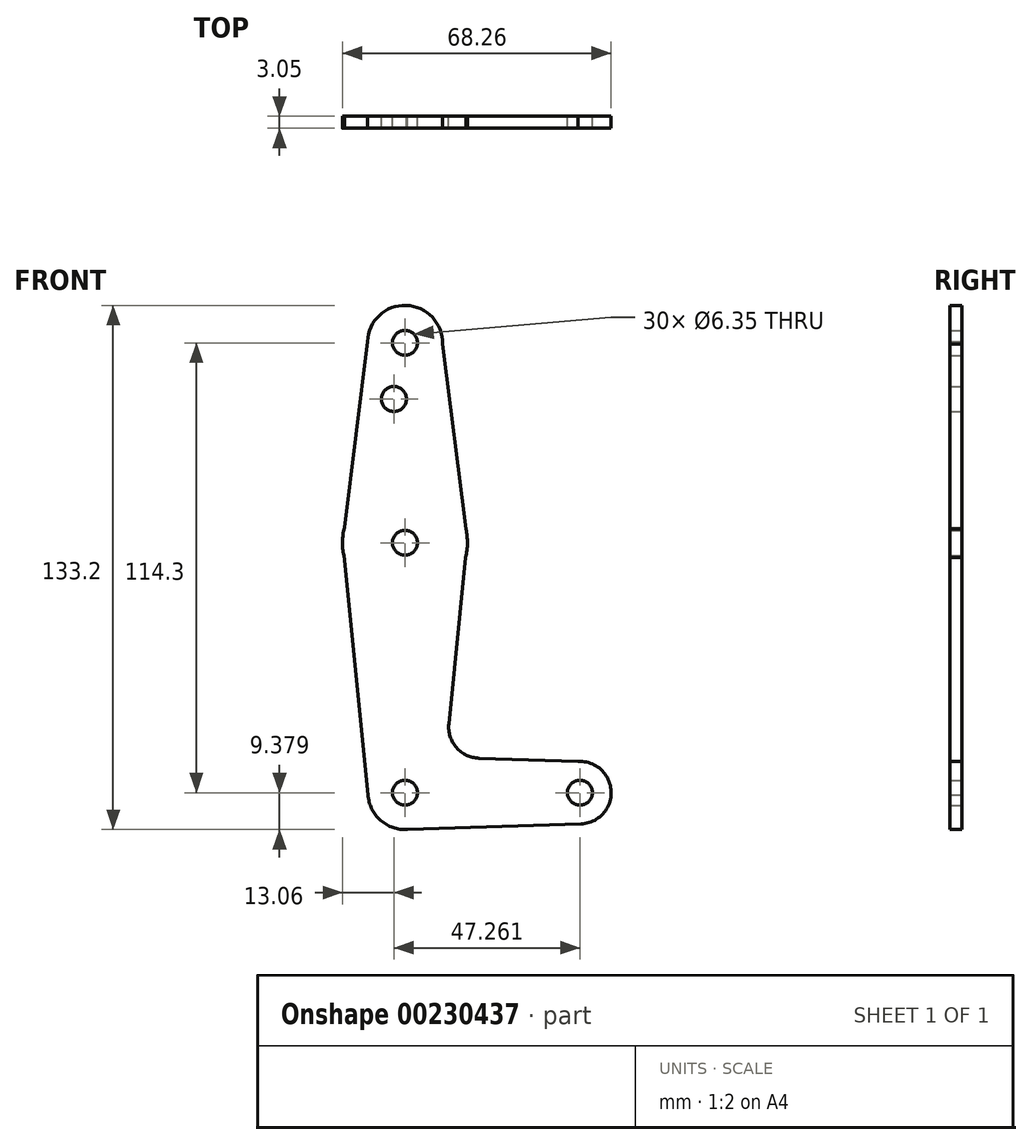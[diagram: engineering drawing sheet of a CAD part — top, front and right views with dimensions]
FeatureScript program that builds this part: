
annotation { "Feature Type Name" : "Feature", "Feature Type Description" : "" }
export const myFeature = defineFeature(function(context is Context, id is Id, definition is map)
    precondition{}
    {
        {
            var Q0;
            Q0=qCreatedBy(makeId("Front.planeOp"),FACE);
            var sketch = newSketch(context, id + "F0", { "sketchPlane" : qUnion([Q0])});
            skLineSegment(sketch, "E0", {"start": v(-33.8, 83.3) * mm, "end": v(-33.8, -31) * mm, "construction": true});
            skLineSegment(sketch, "E1", {"start": v(-33.8, -31) * mm, "end": v(10.65, -31) * mm, "construction": true});
            skCircle(sketch, "E2", {"center": v(-33.8, 32.5) * mm, "radius": 15.88 * mm});
            skCircle(sketch, "E3", {"center": v(-33.8, 83.3) * mm, "radius": 9.52 * mm});
            skCircle(sketch, "E4", {"center": v(-33.8, -31) * mm, "radius": 9.38 * mm});
            skCircle(sketch, "E5", {"center": v(10.65, -31) * mm, "radius": 7.94 * mm});
            skLineSegment(sketch, "E6", {"start": v(-43.32, 83.65) * mm, "end": v(-49.67, 32.56) * mm});
            skLineSegment(sketch, "E7", {"start": v(-33.8, -40.38) * mm, "end": v(10.9, -38.93) * mm});
            skLineSegment(sketch, "E8", {"start": v(10.2, -23.08) * mm, "end": v(-15, -22.24) * mm});
            skLineSegment(sketch, "E9", {"start": v(-22.64, -13.5) * mm, "end": v(-17.93, 33.01) * mm});
            skLineSegment(sketch, "E10", {"start": v(-43.16, -31.53) * mm, "end": v(-49.67, 32.56) * mm});
            skCircle(sketch, "E11", {"center": v(-33.8, 83.3) * mm, "radius": 3.18 * mm});
            skCircle(sketch, "E12", {"center": v(10.65, -31) * mm, "radius": 3.18 * mm});
            skLineSegment(sketch, "E13", {"start": v(-24.28, 83.01) * mm, "end": v(-17.93, 33.01) * mm});
            skCircle(sketch, "E14", {"center": v(-33.8, 32.5) * mm, "radius": 3.18 * mm});
            skCircle(sketch, "E15", {"center": v(-36.6, 69.02) * mm, "radius": 3.18 * mm});
            skCircle(sketch, "E16", {"center": v(-33.8, -31) * mm, "radius": 3.18 * mm});
            skArc(sketch, "E17.filletArc", {"start": v(-22.64, -13.5) * mm, "mid": v(-20.72, -19.53) * mm, "end": v(-15, -22.24) * mm});
            skSolve(sketch);
        }
        {
            var Q0;
            Q0 = qSketchRegion(id + "F0", true);
            extrude(context, id + "F1", {"entities" : qUnion([Q0]), "depth" : 3.05 * mm});
        }
    });
